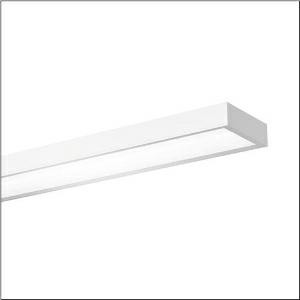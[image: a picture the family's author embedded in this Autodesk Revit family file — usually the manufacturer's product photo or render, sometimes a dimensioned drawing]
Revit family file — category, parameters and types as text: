
# Revit family: sport_31_51hs12dc3dca
name_source: partatom
category: Lighting Fixtures
units: mm (PartAtom-declared; Revit-internal decimal feet)

## family parameters
Cut with Voids When Loaded = No
Host = Face
Light Source = No
Part Type = Normal
Room Calculation Point = No
Round Connector Dimension = Use Diameter
Shared = No

## types (1)
- --- (1 x LED, 7500 lm, 55.4 W, 3000K)
    Apparent Load = 55 VA
    CIE Flux Codes = 65 89 97 100 100
    Color Rendering = 80
    Color Temperature = 3000K
    Default Elevation = 1800 mm
    Description = Sport 31, LED high bay luminaire, primary light control with reflector, of sheet steel, primary anti-glare with prismatic structure, of PC, primary optical cover: cover panel, of PC, light emission: direct distribution, primary light characteristic: symmetric, installation type: suspended mounting, recessed, surface-mounted, LED, rated luminous flux: 7.500lm, luminous efficacy: 130lm/W, light colour: 830, colour temperature: 3000K, control gear: ECG DALI, with terminal, 5-pole, max. 2.5mm², mains connection: 220..240V, AC, 50/60Hz, rated input power: 58W, housing, of sheet steel, traffic white (RAL 9016), length: 1.540mm, width: 315mm, height: 95mm, protection rating (complete): IP20, protection rating (lamp compartment, on room side): IP50, insulation class (complete): insulation class I (protective earthing), certification: CE, ENEC, UKCA, ball protection: ball impact resistant with ceiling mounting or chain suspension, impact resistance: IK08, permissible operating ambient temperature: -20..+35°C, standard: DIN 18032-3, packaging unit: 1 piece
    Height = 100 mm  [stored 0.328084 ft]
    Lamp = 1 x LED
    Lamp Light Flux = 7500 lm
    Lamp Power = 55.4 W
    Lamp count = 1
    Length = 1500 mm
    Luminous efficacy = 135 lm/W
    Manufacturer = Siteco
    ModVariant = No
    Model = 51HS12DC3DCA
    Mounting Place = Ceiling
    Mounting Type = Pendant
    Number of Poles = 1
    OnlyDefault = Yes
    Power Factor = 1
    Product Name = Sport 31
    Product group = LED high bay luminaire
    ProductGroupID = 903
    Protection Class = Protection class I
    Protection Degree = IP 20
    RLX_Detail_Level = 1
    RlxData = <blob elided: 22829 chars, md5=f8c6553b>
    Socket = socket
    Standby Power = 0 W
    System Light Flux = 7500 lm
    System Power = 55 W
    Type Comments = factory setting: luminous flux: 100 % | dim-lin: 254 | 234 mA
    Type Image = l_1006823.jpg
    URL = http://relux.com
    VarID = @adj_121181
    Voltage = 0 V
    Weight = 0.00 kg
    Width = 315 mm

note: [stored X ft] marks values corroborated as IEEE doubles in the binary element streams (Revit-internal decimal feet)

## geometry (parser evidence)
native form markers: Blend x4, Sweep x9
no freeform markers — native parametric forms only
